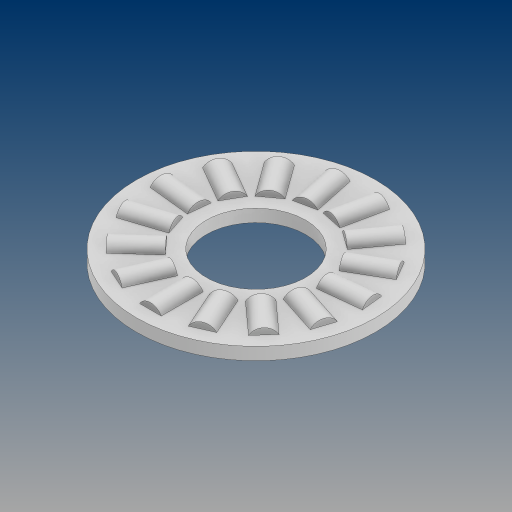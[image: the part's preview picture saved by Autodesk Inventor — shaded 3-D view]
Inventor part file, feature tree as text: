
AUTODESK INVENTOR PART (.ipt)
format: ipt  version: 2024.3 (Build 283343000, 343)  size: 283,136 bytes
history: native  units: in
note: dims shown in document units (in); Inventor stores cm internally (conversion verified against a paired STEP export)
features: other x14, revolve x1, pattern_circular x1
ambient origin geometry x8: Origin, YZ Plane, XZ Plane, XY Plane, X Axis, Y Axis, Z Axis, Center Point
bodies: Solid1 (feature_tree), Solid2 (feature_tree), Solid3 (feature_tree), Solid4 (feature_tree), Solid5 (feature_tree), Solid6 (feature_tree), Solid7 (feature_tree), Solid8 (feature_tree), Solid9 (feature_tree), Solid10 (feature_tree), Solid11 (feature_tree), Solid12 (feature_tree), Solid13 (feature_tree), Solid14 (feature_tree), Solid15 (feature_tree), Solid16 (feature_tree)
feature tree (16):
  revolve  "Revolve2"  [1 undecoded]
  other  "CirPattern1[1]"
  other  "CirPattern1[2]"
  other  "CirPattern1[3]"
  other  "CirPattern1[4]"
  other  "CirPattern1[5]"
  other  "CirPattern1[6]"
  other  "CirPattern1[7]"
  other  "CirPattern1[8]"
  other  "CirPattern1[9]"
  other  "CirPattern1[10]"
  other  "CirPattern1[11]"
  other  "CirPattern1[12]"
  other  "CirPattern1[13]"
  other  "CirPattern1[14]"
  pattern_circular  "CirPattern2"
note: 1 required parameter value undecoded (feature->parameter linkage not recoverable at this tier; creation-order binding heuristic only, values carry confidence <= 0.55)
